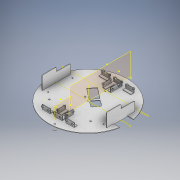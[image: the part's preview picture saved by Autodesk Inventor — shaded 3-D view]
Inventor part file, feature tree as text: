
AUTODESK INVENTOR PART (.ipt)
format: ipt  version: 2020 (Build 240168000, 168)  size: 616,448 bytes
history: native  units: mm
features: sketch x10, other x5, plane x3
ambient origin geometry x8: Origin, YZ Plane, XZ Plane, XY Plane, X Axis, Y Axis, Z Axis, Center Point
bodies: Solid1 (feature_tree)
feature tree (18):
  other  "Gornja_konstrukcija_s_držačima_assembly.iam"
  other  "GornjaKonstrukcija_lidari_kamere_v.2.0.ipt:1"
  other  "5DržačaLidara.ipt:1"
  other  "5DržačaLidara.ipt:2"
  plane  "Work Plane1"
  plane  "Work Plane1_1"
  plane  "Work Plane3"
  other  "Work Axis1"
  sketch  "Sketch8"
  sketch  "Sketch8_1"  dims[d0=10.0mm]
  sketch  "Sketch8_2"
  sketch  "Sketch8_3"
  sketch  "Sketch8_4"
  sketch  "Sketch8_5"
  sketch  "Sketch8_1_1"
  sketch  "Sketch8_2_1"
  sketch  "Sketch8_3_1"
  sketch  "Sketch8_4_1"
